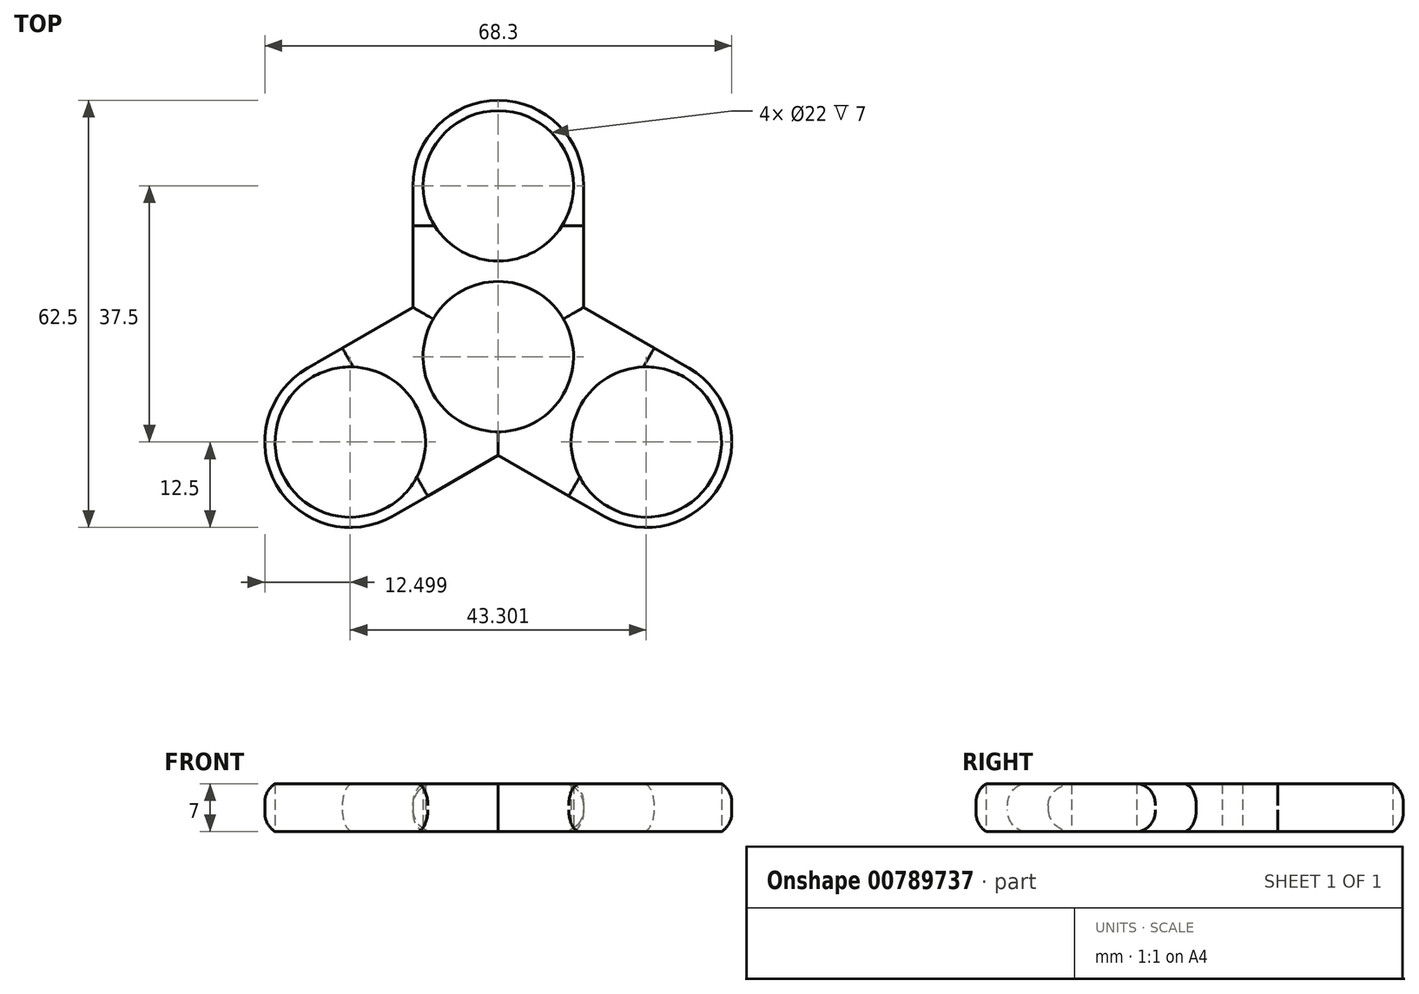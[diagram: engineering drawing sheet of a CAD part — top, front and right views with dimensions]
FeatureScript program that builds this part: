
annotation { "Feature Type Name" : "Feature", "Feature Type Description" : "" }
export const myFeature = defineFeature(function(context is Context, id is Id, definition is map)
    precondition{}
    {
        {
            var Q0;
            Q0=qCreatedBy(makeId("Top.planeOp"),FACE);
            var sketch = newSketch(context, id + "F0", { "sketchPlane" : qUnion([Q0])});
            skCircle(sketch, "E0", {"center": v(0, 0) * mm, "radius": 11 * mm});
            skCircle(sketch, "E1", {"center": v(0, 0) * mm, "radius": 12.5 * mm});
            skLineSegment(sketch, "E2", {"start": v(0, 0) * mm, "end": v(0, 25) * mm});
            skCircle(sketch, "E3", {"center": v(0, 25) * mm, "radius": 12.5 * mm});
            skCircle(sketch, "E4", {"center": v(0, 25) * mm, "radius": 11 * mm});
            skLineSegment(sketch, "E5", {"start": v(-12.5, 0) * mm, "end": v(-12.5, 25) * mm});
            skLineSegment(sketch, "E6", {"start": v(12.5, 0) * mm, "end": v(12.5, 25) * mm});
            skCircle(sketch, "E7.1.0", {"center": v(-21.65, -12.5) * mm, "radius": 11 * mm});
            skCircle(sketch, "E7.1.1", {"center": v(-21.65, -12.5) * mm, "radius": 12.5 * mm});
            skLineSegment(sketch, "E7.1.2", {"start": v(6.25, -10.83) * mm, "end": v(-15.4, -23.33) * mm});
            skLineSegment(sketch, "E7.1.3", {"start": v(-6.25, 10.83) * mm, "end": v(-27.9, -1.67) * mm});
            skCircle(sketch, "E7.2.0", {"center": v(21.65, -12.5) * mm, "radius": 11 * mm});
            skCircle(sketch, "E7.2.1", {"center": v(21.65, -12.5) * mm, "radius": 12.5 * mm});
            skLineSegment(sketch, "E7.2.2", {"start": v(6.25, 10.83) * mm, "end": v(27.9, -1.67) * mm});
            skLineSegment(sketch, "E7.2.3", {"start": v(-6.25, -10.83) * mm, "end": v(15.4, -23.33) * mm});
            skSolve(sketch);
        }
        {
            var Q0;
            Q0=makeQuery(id+"F0.imprint","IMPRINT",FACE,{"disambiguationData":[TD([[makeQuery(id+"F0.imprint","IMPRINT",EDGE,{"derivedFrom":sQuery(id+"F0.wireOp",EDGE,"E4")}),-1.0]])]});
            var Q1;
            {var subQ0=sQuery(id+"F0.wireOp",EDGE,"E5");var subQ1=sQuery(id+"F0.wireOp",EDGE,"E3");var subQ2=makeQuery(id+"F0.imprint","INTERSECT",VERTEX,{"derivedFrom":[subQ1,subQ0]});Q1=makeQuery(id+"F0.imprint","IMPRINT",FACE,{"disambiguationData":[TD([[makeQuery(id+"F0.imprint","IMPRINT",EDGE,{"disambiguationData":[TD([[subQ2,-1.0]])],"derivedFrom":subQ1}),-1.0]])]});}
            var Q2;
            {var subQ0=sQuery(id+"F0.wireOp",EDGE,"E6");var subQ1=sQuery(id+"F0.wireOp",EDGE,"E3");var subQ2=makeQuery(id+"F0.imprint","INTERSECT",VERTEX,{"derivedFrom":[subQ1,subQ0]});Q2=makeQuery(id+"F0.imprint","IMPRINT",FACE,{"disambiguationData":[TD([[makeQuery(id+"F0.imprint","IMPRINT",EDGE,{"disambiguationData":[TD([[subQ2,1.0]])],"derivedFrom":subQ1}),-1.0]])]});}
            var Q3;
            Q3=makeQuery(id+"F0.imprint","IMPRINT",FACE,{"disambiguationData":[TD([[makeQuery(id+"F0.imprint","IMPRINT",EDGE,{"derivedFrom":sQuery(id+"F0.wireOp",EDGE,"E0")}),-1.0]])]});
            var Q4;
            {var subQ0=sQuery(id+"F0.wireOp",EDGE,"E1");var subQ1=sQuery(id+"F0.wireOp",EDGE,"E6");var subQ2=makeQuery(id+"F0.imprint","INTERSECT",VERTEX,{"derivedFrom":[subQ1,subQ0]});Q4=makeQuery(id+"F0.imprint","IMPRINT",FACE,{"disambiguationData":[TD([[makeQuery(id+"F0.imprint","IMPRINT",EDGE,{"disambiguationData":[TD([[subQ2,-1.0]])],"derivedFrom":subQ1}),1.0]])]});}
            var Q5;
            {var subQ0=sQuery(id+"F0.wireOp",EDGE,"E1");var subQ1=sQuery(id+"F0.wireOp",EDGE,"E6");var subQ2=makeQuery(id+"F0.imprint","INTERSECT",VERTEX,{"derivedFrom":[subQ1,subQ0]});Q5=makeQuery(id+"F0.imprint","IMPRINT",FACE,{"disambiguationData":[TD([[makeQuery(id+"F0.imprint","IMPRINT",EDGE,{"disambiguationData":[TD([[subQ2,-1.0]])],"derivedFrom":subQ1}),-1.0]])]});}
            var Q6;
            {var subQ0=sQuery(id+"F0.wireOp",EDGE,"E1");var subQ1=sQuery(id+"F0.wireOp",EDGE,"E7.1.2");var subQ2=makeQuery(id+"F0.imprint","INTERSECT",VERTEX,{"derivedFrom":[subQ1,subQ0]});Q6=makeQuery(id+"F0.imprint","IMPRINT",FACE,{"disambiguationData":[TD([[makeQuery(id+"F0.imprint","IMPRINT",EDGE,{"disambiguationData":[TD([[subQ2,-1.0]])],"derivedFrom":subQ1}),1.0]])]});}
            var Q7;
            {var subQ0=sQuery(id+"F0.wireOp",EDGE,"E7.1.2");var subQ1=sQuery(id+"F0.wireOp",EDGE,"E7.1.1");var subQ2=makeQuery(id+"F0.imprint","INTERSECT",VERTEX,{"derivedFrom":[subQ1,subQ0]});Q7=makeQuery(id+"F0.imprint","IMPRINT",FACE,{"disambiguationData":[TD([[makeQuery(id+"F0.imprint","IMPRINT",EDGE,{"disambiguationData":[TD([[subQ2,-1.0]])],"derivedFrom":subQ1}),-1.0]])]});}
            var Q8;
            {var subQ0=sQuery(id+"F0.wireOp",EDGE,"E1");var subQ1=sQuery(id+"F0.wireOp",EDGE,"E7.1.2");var subQ2=makeQuery(id+"F0.imprint","INTERSECT",VERTEX,{"derivedFrom":[subQ1,subQ0]});Q8=makeQuery(id+"F0.imprint","IMPRINT",FACE,{"disambiguationData":[TD([[makeQuery(id+"F0.imprint","IMPRINT",EDGE,{"disambiguationData":[TD([[subQ2,-1.0]])],"derivedFrom":subQ1}),-1.0]])]});}
            var Q9;
            {var subQ0=sQuery(id+"F0.wireOp",EDGE,"E1");var subQ1=sQuery(id+"F0.wireOp",EDGE,"E5");var subQ2=makeQuery(id+"F0.imprint","INTERSECT",VERTEX,{"derivedFrom":[subQ1,subQ0]});Q9=makeQuery(id+"F0.imprint","IMPRINT",FACE,{"disambiguationData":[TD([[makeQuery(id+"F0.imprint","IMPRINT",EDGE,{"disambiguationData":[TD([[subQ2,-1.0]])],"derivedFrom":subQ1}),-1.0]])]});}
            var Q10;
            {var subQ0=sQuery(id+"F0.wireOp",EDGE,"E1");var subQ1=sQuery(id+"F0.wireOp",EDGE,"E5");var subQ2=makeQuery(id+"F0.imprint","INTERSECT",VERTEX,{"derivedFrom":[subQ1,subQ0]});Q10=makeQuery(id+"F0.imprint","IMPRINT",FACE,{"disambiguationData":[TD([[makeQuery(id+"F0.imprint","IMPRINT",EDGE,{"disambiguationData":[TD([[subQ2,-1.0]])],"derivedFrom":subQ1}),1.0]])]});}
            var Q11;
            Q11=makeQuery(id+"F0.imprint","IMPRINT",FACE,{"disambiguationData":[TD([[makeQuery(id+"F0.imprint","IMPRINT",EDGE,{"derivedFrom":sQuery(id+"F0.wireOp",EDGE,"E7.1.0")}),-1.0]])]});
            var Q12;
            Q12=makeQuery(id+"F0.imprint","IMPRINT",FACE,{"disambiguationData":[TD([[makeQuery(id+"F0.imprint","IMPRINT",EDGE,{"derivedFrom":sQuery(id+"F0.wireOp",EDGE,"E7.2.0")}),-1.0]])]});
            extrude(context, id + "F1", {"entities" : qUnion([Q0, Q1, Q2, Q3, Q4, Q5, Q6, Q7, Q8, Q9, Q10, Q11, Q12]), "depth" : 7 * mm, "offsetDistance" : 25 * mm});
        }
        {
            var Q0;
            Q0=makeQuery(id+"F1.opExtrude","CAP_EDGE",EDGE,{"disambiguationData":[OSD([sQuery(id+"F0.wireOp",EDGE,"E5")])],"isStart":false});
            var Q1;
            Q1=makeQuery(id+"F1.opExtrude","CAP_EDGE",EDGE,{"disambiguationData":[OSD([sQuery(id+"F0.wireOp",EDGE,"E7.1.3")])],"isStart":false});
            var Q2;
            Q2=makeQuery(id+"F1.opExtrude","CAP_EDGE",EDGE,{"disambiguationData":[OSD([sQuery(id+"F0.wireOp",EDGE,"E7.2.3")])],"isStart":true});
            var Q3;
            Q3=makeQuery(id+"F1.opExtrude","CAP_EDGE",EDGE,{"disambiguationData":[OSD([sQuery(id+"F0.wireOp",EDGE,"E7.2.2")])],"isStart":false});
            var Q4;
            Q4=makeQuery(id+"F1.opExtrude","CAP_EDGE",EDGE,{"disambiguationData":[OSD([sQuery(id+"F0.wireOp",EDGE,"E7.1.3")])],"isStart":true});
            var Q5;
            Q5=makeQuery(id+"F1.opExtrude","CAP_EDGE",EDGE,{"disambiguationData":[OSD([sQuery(id+"F0.wireOp",EDGE,"E5")])],"isStart":true});
            fillet(context, id + "F2", {"entities" : qUnion([Q0, Q1, Q2, Q3, Q4, Q5]), "radius" : 3.2 * mm, "tangentPropagation" : true, "allowEdgeOverflow" : false});
        }
    });
